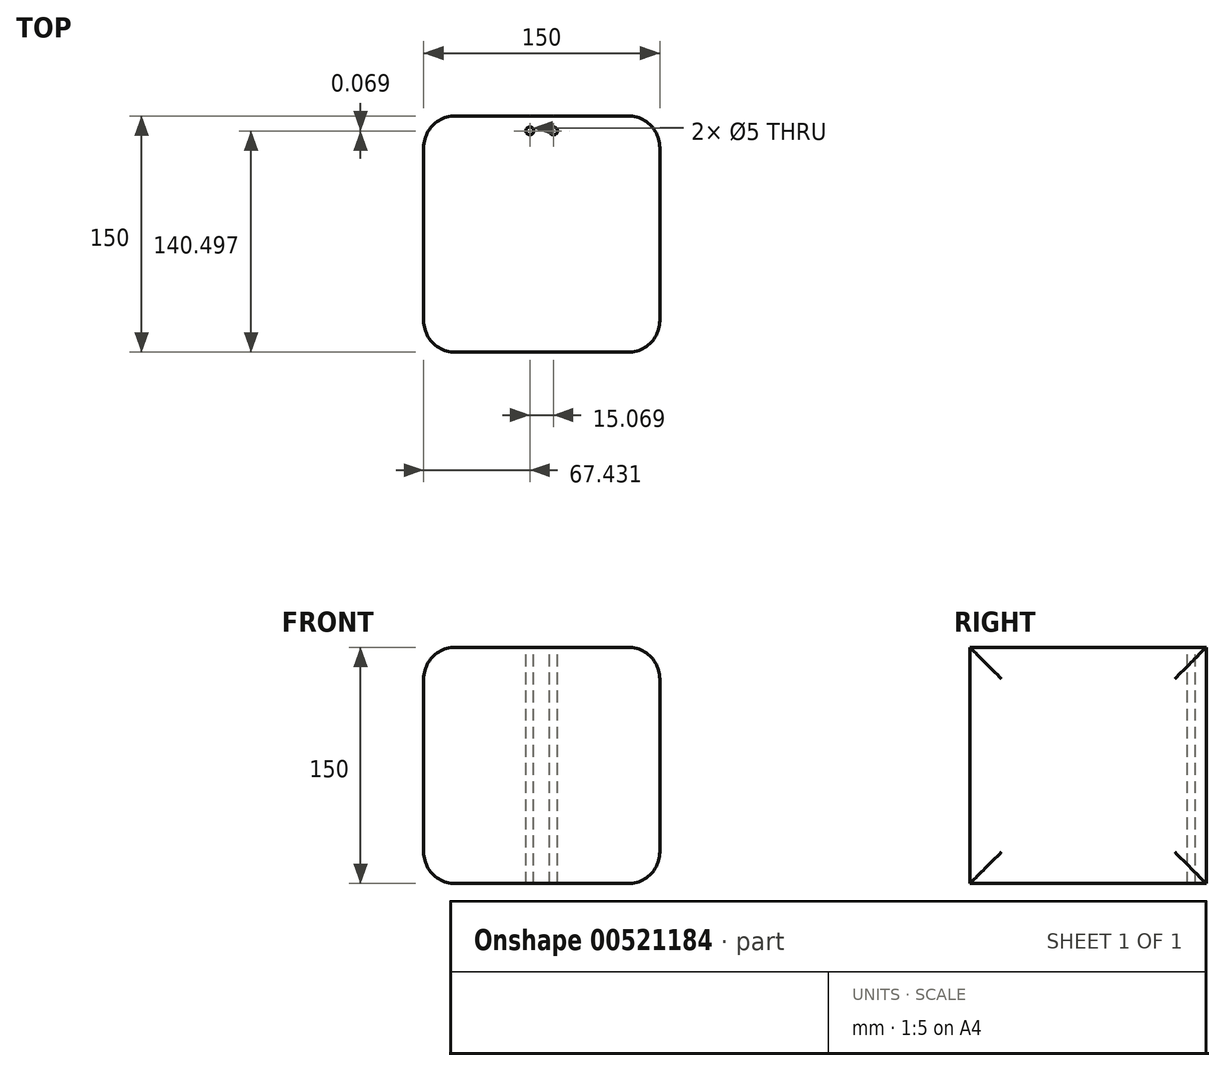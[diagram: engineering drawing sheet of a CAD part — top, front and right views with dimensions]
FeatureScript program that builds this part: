
annotation { "Feature Type Name" : "Feature", "Feature Type Description" : "" }
export const myFeature = defineFeature(function(context is Context, id is Id, definition is map)
    precondition{}
    {
        {
            var Q0;
            Q0=qCreatedBy(makeId("Top.planeOp"),FACE);
            var sketch = newSketch(context, id + "F0", { "sketchPlane" : qUnion([Q0])});
            skLineSegment(sketch, "E0.bottom", {"start": v(-75, 85.64) * mm, "end": v(75, 85.64) * mm});
            skLineSegment(sketch, "E0.top", {"start": v(-75, -64.36) * mm, "end": v(75, -64.36) * mm});
            skLineSegment(sketch, "E0.left", {"start": v(-75, 85.64) * mm, "end": v(-75, -64.36) * mm});
            skLineSegment(sketch, "E0.right", {"start": v(75, 85.64) * mm, "end": v(75, -64.36) * mm});
            skSolve(sketch);
        }
        {
            var Q0;
            Q0=makeQuery(id+"F0.imprint","IMPRINT",FACE,{"disambiguationData":[TD([[makeQuery(id+"F0.imprint","IMPRINT",EDGE,{"derivedFrom":sQuery(id+"F0.wireOp",EDGE,"E0.bottom")}),-1.0]])]});
            extrude(context, id + "F1", {"entities" : qUnion([Q0]), "oppositeDirection" : true, "depth" : 150 * mm, "offsetDistance" : 25 * mm});
        }
        {
            var Q0;
            Q0=makeQuery(id+"F1.opExtrude","SWEPT_FACE",FACE,{"disambiguationData":[OSD([sQuery(id+"F0.wireOp",EDGE,"E0.left")])]});
            var Q1;
            Q1=makeQuery(id+"F1.opExtrude","SWEPT_FACE",FACE,{"disambiguationData":[OSD([sQuery(id+"F0.wireOp",EDGE,"E0.right")])]});
            fillet(context, id + "F2", {"entities" : qUnion([Q0, Q1]), "radius" : 20 * mm, "tangentPropagation" : true, "allowEdgeOverflow" : false});
        }
        {
            var Q0;
            Q0=makeQuery(id+"F1.opExtrude","CAP_FACE",FACE,{"disambiguationData":[OSD([sQuery(id+"F0.wireOp",EDGE,"E0.bottom"),sQuery(id+"F0.wireOp",EDGE,"E0.top"),sQuery(id+"F0.wireOp",EDGE,"E0.left"),sQuery(id+"F0.wireOp",EDGE,"E0.right")])],"isStart":true});
            var sketch = newSketch(context, id + "F3", { "sketchPlane" : qUnion([Q0])});
            skCircle(sketch, "E1", {"center": v(-7.57, 76.2) * mm, "radius": 2.43 * mm});
            skCircle(sketch, "E2", {"center": v(7.5, 76.14) * mm, "radius": 2.5 * mm});
            skSolve(sketch);
        }
        {
            var Q0;
            Q0=sQuery(id+"F3.wireOp",VERTEX,"E2.center");
            var Q1;
            Q1=sQuery(id+"F3.wireOp",VERTEX,"E1.center");
            var Q2;
            Q2=makeQuery(id+"F1.opExtrude","SWEPT_BODY",BODY,{"disambiguationData":[OSD([sQuery(id+"F0.wireOp",EDGE,"E0.bottom"),sQuery(id+"F0.wireOp",EDGE,"E0.top"),sQuery(id+"F0.wireOp",EDGE,"E0.left"),sQuery(id+"F0.wireOp",EDGE,"E0.right")])]});
            hole(context, id + "F4", {"style" : HoleStyle.SIMPLE, "endStyle" : HoleEndStyle.THROUGH, "holeDiameter" : 5 * mm, "isTappedThrough" : true, "tappedDepth" : 12 * mm, "tapClearance" : 3, "locations" : qUnion([Q0, Q1]), "scope" : qUnion([Q2])});
        }
    });
